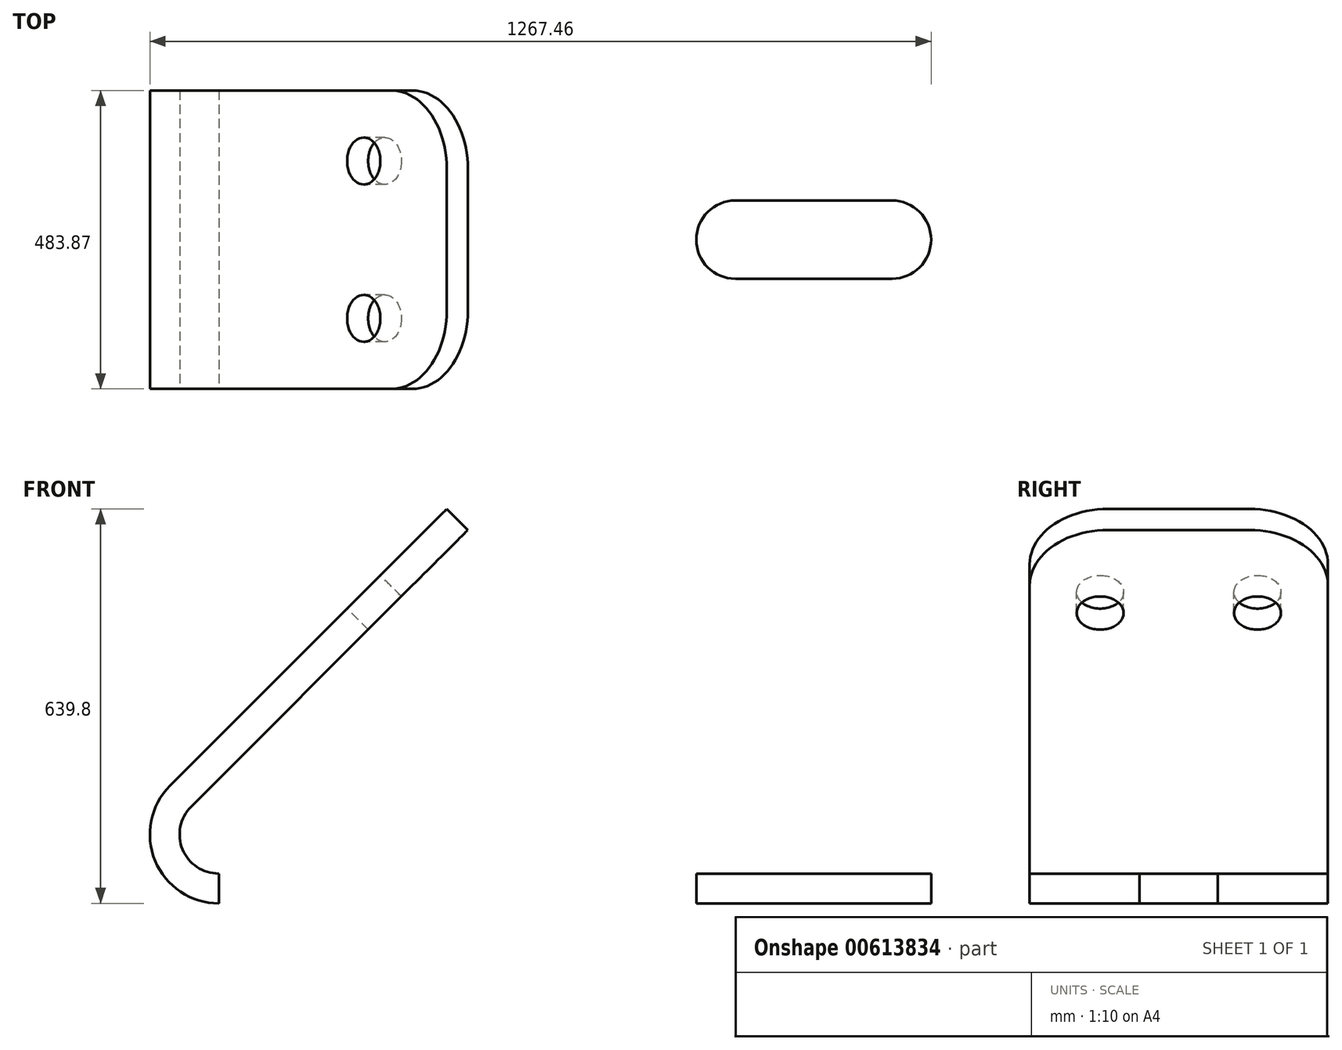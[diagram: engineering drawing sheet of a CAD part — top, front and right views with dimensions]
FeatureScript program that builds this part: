
annotation { "Feature Type Name" : "Feature", "Feature Type Description" : "" }
export const myFeature = defineFeature(function(context is Context, id is Id, definition is map)
    precondition{}
    {
        {
            var Q0;
            Q0=qCreatedBy(makeId("Front.planeOp"),FACE);
            var sketch = newSketch(context, id + "F0", { "sketchPlane" : qUnion([Q0])});
            skLineSegment(sketch, "E0", {"start": v(0, 0) * mm, "end": v(0, 48.26) * mm});
            skLineSegment(sketch, "E1", {"start": v(0, 48.26) * mm, "end": v(-1270, 48.26) * mm});
            skLineSegment(sketch, "E2", {"start": v(0, 0) * mm, "end": v(-1270, 0) * mm});
            skArc(sketch, "E3", {"start": v(-1349.03, 190.79) * mm, "mid": v(-1373.25, 69) * mm, "end": v(-1270, 0) * mm});
            skArc(sketch, "E4", {"start": v(-1314.9, 156.66) * mm, "mid": v(-1328.67, 87.46) * mm, "end": v(-1270, 48.26) * mm});
            skLineSegment(sketch, "E5", {"start": v(-1314.9, 156.66) * mm, "end": v(-865.89, 605.67) * mm});
            skLineSegment(sketch, "E6", {"start": v(-865.89, 605.67) * mm, "end": v(-900.01, 639.8) * mm});
            skLineSegment(sketch, "E7", {"start": v(-900.01, 639.8) * mm, "end": v(-1349.03, 190.79) * mm});
            skSolve(sketch);
        }
        {
            var Q0;
            Q0=makeQuery(id+"F0.imprint","IMPRINT",FACE,{"disambiguationData":[TD([[makeQuery(id+"F0.imprint","IMPRINT",EDGE,{"derivedFrom":sQuery(id+"F0.wireOp",EDGE,"E0")}),1.0]])]});
            extrude(context, id + "F1", {"entities" : qUnion([Q0]), "oppositeDirection" : true, "depth" : 483.87 * mm, "offsetDistance" : 25.4 * mm});
        }
        {
            var Q0;
            Q0=makeQuery(id+"F1.opExtrude","SWEPT_FACE",FACE,{"disambiguationData":[OSD([sQuery(id+"F0.wireOp",EDGE,"E1")])]});
            var sketch = newSketch(context, id + "F2", { "sketchPlane" : qUnion([Q0])});
            skCircle(sketch, "E8", {"center": v(-812.8, 241.93) * mm, "radius": 63.5 * mm});
            skLineSegment(sketch, "E9", {"start": v(-431.8, 241.94) * mm, "end": v(-177.8, 241.94) * mm});
            skPoint(sketch, "E9.startSnap0", {"position": v(-1270, 241.94) * mm});
            skArc(sketch, "E10.0.startCap", {"start": v(-431.8, 178.44) * mm, "mid": v(-495.3, 241.94) * mm, "end": v(-431.8, 305.44) * mm});
            skArc(sketch, "E10.0.endCap", {"start": v(-177.8, 305.44) * mm, "mid": v(-114.3, 241.94) * mm, "end": v(-177.8, 178.44) * mm});
            skLineSegment(sketch, "E10.0.left", {"start": v(-431.8, 305.44) * mm, "end": v(-177.8, 305.44) * mm});
            skLineSegment(sketch, "E10.0.right", {"start": v(-431.8, 178.44) * mm, "end": v(-177.8, 178.44) * mm});
            skSolve(sketch);
        }
        {
            var Q0;
            Q0=makeQuery(id+"F2.imprint","IMPRINT",FACE,{"disambiguationData":[TD([[makeQuery(id+"F2.imprint","IMPRINT",EDGE,{"derivedFrom":sQuery(id+"F2.wireOp",EDGE,"E8")}),1.0]])]});
            var Q1;
            Q1=makeQuery(id+"F2.imprint","IMPRINT",FACE,{"disambiguationData":[TD([[makeQuery(id+"F2.imprint","IMPRINT",EDGE,{"derivedFrom":sQuery(id+"F2.wireOp",EDGE,"E10.0.startCap")}),-1.0]])]});
            extrude(context, id + "F3", {"entities" : qUnion([Q0, Q1]), "operationType" : NewBodyOperationType.REMOVE, "endBound" : BoundingType.THROUGH_ALL, "oppositeDirection" : true, "depth" : 25.4 * mm, "offsetDistance" : 25.4 * mm});
        }
        {
            var Q0;
            Q0=makeQuery(id+"F1.opExtrude","SWEPT_FACE",FACE,{"disambiguationData":[OSD([sQuery(id+"F0.wireOp",EDGE,"E7")])]});
            var sketch = newSketch(context, id + "F4", { "sketchPlane" : qUnion([Q0])});
            skCircle(sketch, "E11", {"center": v(-369.57, -374.5) * mm, "radius": 38.1 * mm});
            skCircle(sketch, "E12", {"center": v(-114.3, -374.5) * mm, "radius": 38.1 * mm});
            skSolve(sketch);
        }
        {
            var Q0;
            Q0 = qSketchRegion(id + "F4", true);
            var Q1;
            Q1=makeQuery(id+"F1.opExtrude","SWEPT_FACE",FACE,{"disambiguationData":[OSD([sQuery(id+"F0.wireOp",EDGE,"E5")])]});
            extrude(context, id + "F5", {"entities" : qUnion([Q0]), "operationType" : NewBodyOperationType.REMOVE, "endBound" : BoundingType.UP_TO_SURFACE, "oppositeDirection" : true, "depth" : 25.4 * mm, "endBoundEntityFace" : qUnion([Q1]), "offsetDistance" : 25.4 * mm});
        }
        {
            var Q0;
            Q0=makeQuery(id+"F1.opExtrude","CAP_EDGE",EDGE,{"disambiguationData":[OSD([sQuery(id+"F0.wireOp",EDGE,"E0")])],"isStart":false});
            var Q1;
            Q1=makeQuery(id+"F1.opExtrude","CAP_EDGE",EDGE,{"disambiguationData":[OSD([sQuery(id+"F0.wireOp",EDGE,"E0")])],"isStart":true});
            var Q2;
            Q2=makeQuery(id+"F1.opExtrude","CAP_EDGE",EDGE,{"disambiguationData":[OSD([sQuery(id+"F0.wireOp",EDGE,"E6")])],"isStart":true});
            var Q3;
            Q3=makeQuery(id+"F1.opExtrude","CAP_EDGE",EDGE,{"disambiguationData":[OSD([sQuery(id+"F0.wireOp",EDGE,"E6")])],"isStart":false});
            fillet(context, id + "F6", {"entities" : qUnion([Q0, Q1, Q2, Q3]), "radius" : 127 * mm, "tangentPropagation" : true, "allowEdgeOverflow" : false});
        }
    });
